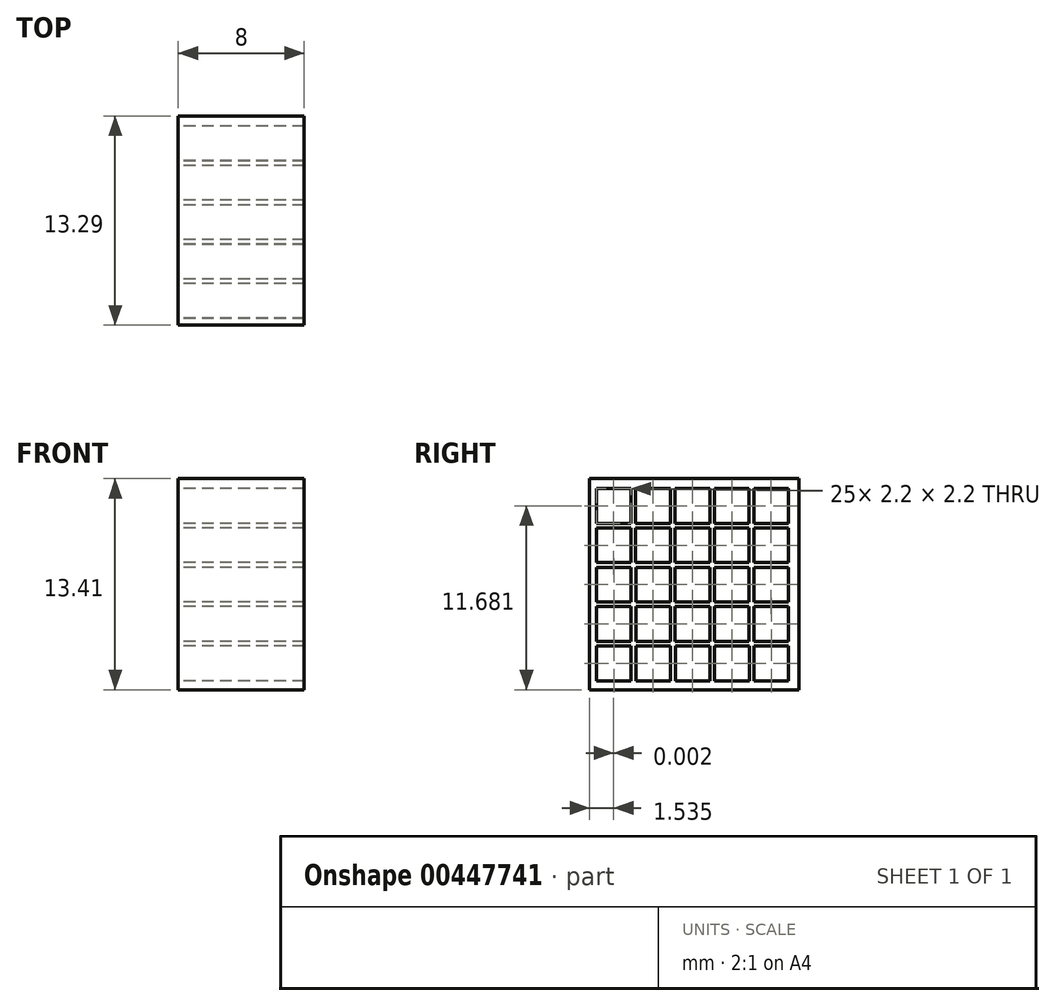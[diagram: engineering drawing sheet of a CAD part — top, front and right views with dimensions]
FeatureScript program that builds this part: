
annotation { "Feature Type Name" : "Feature", "Feature Type Description" : "" }
export const myFeature = defineFeature(function(context is Context, id is Id, definition is map)
    precondition{}
    {
        {
            var Q0;
            Q0=qCreatedBy(makeId("Right.planeOp"),FACE);
            var sketch = newSketch(context, id + "F0", { "sketchPlane" : qUnion([Q0])});
            skLineSegment(sketch, "E0.bottom", {"start": v(-0.5, -2.47) * mm, "end": v(1.7, -2.47) * mm});
            skLineSegment(sketch, "E0.top", {"start": v(-0.5, -4.67) * mm, "end": v(1.7, -4.67) * mm});
            skLineSegment(sketch, "E0.left", {"start": v(-0.5, -2.47) * mm, "end": v(-0.5, -4.67) * mm});
            skLineSegment(sketch, "E0.right", {"start": v(1.7, -2.47) * mm, "end": v(1.7, -4.67) * mm});
            skLineSegment(sketch, "E1.1.0.0", {"start": v(4.2, -2.47) * mm, "end": v(4.2, -4.67) * mm});
            skLineSegment(sketch, "E1.1.0.1", {"start": v(2, -2.47) * mm, "end": v(2, -4.67) * mm});
            skLineSegment(sketch, "E1.1.0.2", {"start": v(2, -4.67) * mm, "end": v(4.2, -4.67) * mm});
            skLineSegment(sketch, "E1.1.0.3", {"start": v(2, -2.47) * mm, "end": v(4.2, -2.47) * mm});
            skLineSegment(sketch, "E1.2.0.0", {"start": v(6.7, -2.47) * mm, "end": v(6.7, -4.67) * mm});
            skLineSegment(sketch, "E1.2.0.1", {"start": v(4.5, -2.47) * mm, "end": v(4.5, -4.67) * mm});
            skLineSegment(sketch, "E1.2.0.2", {"start": v(4.5, -4.67) * mm, "end": v(6.7, -4.67) * mm});
            skLineSegment(sketch, "E1.2.0.3", {"start": v(4.5, -2.47) * mm, "end": v(6.7, -2.47) * mm});
            skLineSegment(sketch, "E1.3.0.0", {"start": v(9.2, -2.47) * mm, "end": v(9.2, -4.67) * mm});
            skLineSegment(sketch, "E1.3.0.1", {"start": v(7, -2.47) * mm, "end": v(7, -4.67) * mm});
            skLineSegment(sketch, "E1.3.0.2", {"start": v(7, -4.67) * mm, "end": v(9.2, -4.67) * mm});
            skLineSegment(sketch, "E1.3.0.3", {"start": v(7, -2.47) * mm, "end": v(9.2, -2.47) * mm});
            skLineSegment(sketch, "E1.4.0.0", {"start": v(11.7, -2.47) * mm, "end": v(11.7, -4.67) * mm});
            skLineSegment(sketch, "E1.4.0.1", {"start": v(9.5, -2.47) * mm, "end": v(9.5, -4.67) * mm});
            skLineSegment(sketch, "E1.4.0.2", {"start": v(9.5, -4.67) * mm, "end": v(11.7, -4.67) * mm});
            skLineSegment(sketch, "E1.4.0.3", {"start": v(9.5, -2.47) * mm, "end": v(11.7, -2.47) * mm});
            skLineSegment(sketch, "E2.1.0.0", {"start": v(11.7, -4.97) * mm, "end": v(11.7, -7.17) * mm});
            skLineSegment(sketch, "E2.1.0.1", {"start": v(9.5, -7.17) * mm, "end": v(11.7, -7.17) * mm});
            skLineSegment(sketch, "E2.1.0.3", {"start": v(9.2, -4.97) * mm, "end": v(9.2, -7.17) * mm});
            skLineSegment(sketch, "E2.1.0.4", {"start": v(4.5, -4.97) * mm, "end": v(6.7, -4.97) * mm});
            skLineSegment(sketch, "E2.1.0.5", {"start": v(4.5, -7.17) * mm, "end": v(6.7, -7.17) * mm});
            skLineSegment(sketch, "E2.1.0.6", {"start": v(4.5, -4.97) * mm, "end": v(4.5, -7.17) * mm});
            skLineSegment(sketch, "E2.1.0.7", {"start": v(6.7, -4.97) * mm, "end": v(6.7, -7.17) * mm});
            skLineSegment(sketch, "E2.1.0.8", {"start": v(2, -4.97) * mm, "end": v(4.2, -4.97) * mm});
            skLineSegment(sketch, "E2.1.0.9", {"start": v(2, -7.17) * mm, "end": v(4.2, -7.17) * mm});
            skLineSegment(sketch, "E2.1.0.10", {"start": v(4.2, -4.97) * mm, "end": v(4.2, -7.17) * mm});
            skLineSegment(sketch, "E2.1.0.11", {"start": v(-0.5, -4.97) * mm, "end": v(-0.5, -7.17) * mm});
            skLineSegment(sketch, "E2.1.0.12", {"start": v(-0.5, -4.97) * mm, "end": v(1.7, -4.97) * mm});
            skLineSegment(sketch, "E2.1.0.13", {"start": v(7, -4.97) * mm, "end": v(9.2, -4.97) * mm});
            skLineSegment(sketch, "E2.1.0.14", {"start": v(7, -7.17) * mm, "end": v(9.2, -7.17) * mm});
            skLineSegment(sketch, "E2.1.0.15", {"start": v(7, -4.97) * mm, "end": v(7, -7.17) * mm});
            skLineSegment(sketch, "E2.1.0.16", {"start": v(9.5, -4.97) * mm, "end": v(9.5, -7.17) * mm});
            skLineSegment(sketch, "E2.1.0.17", {"start": v(9.5, -4.97) * mm, "end": v(11.7, -4.97) * mm});
            skLineSegment(sketch, "E2.1.0.18", {"start": v(1.7, -4.97) * mm, "end": v(1.7, -7.17) * mm});
            skLineSegment(sketch, "E2.1.0.19", {"start": v(-0.5, -7.17) * mm, "end": v(1.7, -7.17) * mm});
            skLineSegment(sketch, "E2.2.0.0", {"start": v(11.7, -7.47) * mm, "end": v(11.7, -9.67) * mm});
            skLineSegment(sketch, "E2.2.0.1", {"start": v(9.5, -9.67) * mm, "end": v(11.7, -9.67) * mm});
            skLineSegment(sketch, "E2.2.0.2", {"start": v(-0.5, -9.67) * mm, "end": v(2, -9.67) * mm, "construction": true});
            skLineSegment(sketch, "E2.2.0.3", {"start": v(9.2, -7.47) * mm, "end": v(9.2, -9.67) * mm});
            skLineSegment(sketch, "E2.2.0.4", {"start": v(4.5, -7.47) * mm, "end": v(6.7, -7.47) * mm});
            skLineSegment(sketch, "E2.2.0.5", {"start": v(4.5, -9.67) * mm, "end": v(6.7, -9.67) * mm});
            skLineSegment(sketch, "E2.2.0.6", {"start": v(4.5, -7.47) * mm, "end": v(4.5, -9.67) * mm});
            skLineSegment(sketch, "E2.2.0.7", {"start": v(6.7, -7.47) * mm, "end": v(6.7, -9.67) * mm});
            skLineSegment(sketch, "E2.2.0.8", {"start": v(2, -7.47) * mm, "end": v(4.2, -7.47) * mm});
            skLineSegment(sketch, "E2.2.0.9", {"start": v(2, -9.67) * mm, "end": v(4.2, -9.67) * mm});
            skLineSegment(sketch, "E2.2.0.10", {"start": v(4.2, -7.47) * mm, "end": v(4.2, -9.67) * mm});
            skLineSegment(sketch, "E2.2.0.11", {"start": v(-0.5, -7.47) * mm, "end": v(-0.5, -9.67) * mm});
            skLineSegment(sketch, "E2.2.0.12", {"start": v(-0.5, -7.47) * mm, "end": v(1.7, -7.47) * mm});
            skLineSegment(sketch, "E2.2.0.13", {"start": v(7, -7.47) * mm, "end": v(9.2, -7.47) * mm});
            skLineSegment(sketch, "E2.2.0.14", {"start": v(7, -9.67) * mm, "end": v(9.2, -9.67) * mm});
            skLineSegment(sketch, "E2.2.0.15", {"start": v(7, -7.47) * mm, "end": v(7, -9.67) * mm});
            skLineSegment(sketch, "E2.2.0.16", {"start": v(9.5, -7.47) * mm, "end": v(9.5, -9.67) * mm});
            skLineSegment(sketch, "E2.2.0.17", {"start": v(9.5, -7.47) * mm, "end": v(11.7, -7.47) * mm});
            skLineSegment(sketch, "E2.2.0.18", {"start": v(1.7, -7.47) * mm, "end": v(1.7, -9.67) * mm});
            skLineSegment(sketch, "E2.2.0.19", {"start": v(-0.5, -9.67) * mm, "end": v(1.7, -9.67) * mm});
            skLineSegment(sketch, "E2.3.0.0", {"start": v(11.7, -9.97) * mm, "end": v(11.7, -12.17) * mm});
            skLineSegment(sketch, "E2.3.0.1", {"start": v(9.5, -12.17) * mm, "end": v(11.7, -12.17) * mm});
            skLineSegment(sketch, "E2.3.0.3", {"start": v(9.2, -9.97) * mm, "end": v(9.2, -12.17) * mm});
            skLineSegment(sketch, "E2.3.0.4", {"start": v(4.5, -9.97) * mm, "end": v(6.7, -9.97) * mm});
            skLineSegment(sketch, "E2.3.0.5", {"start": v(4.5, -12.17) * mm, "end": v(6.7, -12.17) * mm});
            skLineSegment(sketch, "E2.3.0.6", {"start": v(4.5, -9.97) * mm, "end": v(4.5, -12.17) * mm});
            skLineSegment(sketch, "E2.3.0.7", {"start": v(6.7, -9.97) * mm, "end": v(6.7, -12.17) * mm});
            skLineSegment(sketch, "E2.3.0.8", {"start": v(2, -9.97) * mm, "end": v(4.2, -9.97) * mm});
            skLineSegment(sketch, "E2.3.0.9", {"start": v(2, -12.17) * mm, "end": v(4.2, -12.17) * mm});
            skLineSegment(sketch, "E2.3.0.10", {"start": v(4.2, -9.97) * mm, "end": v(4.2, -12.17) * mm});
            skLineSegment(sketch, "E2.3.0.11", {"start": v(-0.5, -9.97) * mm, "end": v(-0.5, -12.17) * mm});
            skLineSegment(sketch, "E2.3.0.12", {"start": v(-0.5, -9.97) * mm, "end": v(1.7, -9.97) * mm});
            skLineSegment(sketch, "E2.3.0.13", {"start": v(7, -9.97) * mm, "end": v(9.2, -9.97) * mm});
            skLineSegment(sketch, "E2.3.0.14", {"start": v(7, -12.17) * mm, "end": v(9.2, -12.17) * mm});
            skLineSegment(sketch, "E2.3.0.15", {"start": v(7, -9.97) * mm, "end": v(7, -12.17) * mm});
            skLineSegment(sketch, "E2.3.0.16", {"start": v(9.5, -9.97) * mm, "end": v(9.5, -12.17) * mm});
            skLineSegment(sketch, "E2.3.0.17", {"start": v(9.5, -9.97) * mm, "end": v(11.7, -9.97) * mm});
            skLineSegment(sketch, "E2.3.0.18", {"start": v(1.7, -9.97) * mm, "end": v(1.7, -12.17) * mm});
            skLineSegment(sketch, "E2.3.0.19", {"start": v(-0.5, -12.17) * mm, "end": v(1.7, -12.17) * mm});
            skLineSegment(sketch, "E2.4.0.0", {"start": v(11.7, -12.47) * mm, "end": v(11.7, -14.67) * mm});
            skLineSegment(sketch, "E2.4.0.1", {"start": v(9.5, -14.67) * mm, "end": v(11.7, -14.67) * mm});
            skLineSegment(sketch, "E2.4.0.2", {"start": v(-0.5, -14.67) * mm, "end": v(2, -14.67) * mm, "construction": true});
            skLineSegment(sketch, "E2.4.0.3", {"start": v(9.2, -12.47) * mm, "end": v(9.2, -14.67) * mm});
            skLineSegment(sketch, "E2.4.0.4", {"start": v(4.5, -12.47) * mm, "end": v(6.7, -12.47) * mm});
            skLineSegment(sketch, "E2.4.0.5", {"start": v(4.5, -14.67) * mm, "end": v(6.7, -14.67) * mm});
            skLineSegment(sketch, "E2.4.0.6", {"start": v(4.5, -12.47) * mm, "end": v(4.5, -14.67) * mm});
            skLineSegment(sketch, "E2.4.0.7", {"start": v(6.7, -12.47) * mm, "end": v(6.7, -14.67) * mm});
            skLineSegment(sketch, "E2.4.0.8", {"start": v(2, -12.47) * mm, "end": v(4.2, -12.47) * mm});
            skLineSegment(sketch, "E2.4.0.9", {"start": v(2, -14.67) * mm, "end": v(4.2, -14.67) * mm});
            skLineSegment(sketch, "E2.4.0.10", {"start": v(4.2, -12.47) * mm, "end": v(4.2, -14.67) * mm});
            skLineSegment(sketch, "E2.4.0.11", {"start": v(-0.5, -12.47) * mm, "end": v(-0.5, -14.67) * mm});
            skLineSegment(sketch, "E2.4.0.12", {"start": v(-0.5, -12.47) * mm, "end": v(1.7, -12.47) * mm});
            skLineSegment(sketch, "E2.4.0.13", {"start": v(7, -12.47) * mm, "end": v(9.2, -12.47) * mm});
            skLineSegment(sketch, "E2.4.0.14", {"start": v(7, -14.67) * mm, "end": v(9.2, -14.67) * mm});
            skLineSegment(sketch, "E2.4.0.15", {"start": v(7, -12.47) * mm, "end": v(7, -14.67) * mm});
            skLineSegment(sketch, "E2.4.0.16", {"start": v(9.5, -12.47) * mm, "end": v(9.5, -14.67) * mm});
            skLineSegment(sketch, "E2.4.0.17", {"start": v(9.5, -12.47) * mm, "end": v(11.7, -12.47) * mm});
            skLineSegment(sketch, "E2.4.0.18", {"start": v(1.7, -12.47) * mm, "end": v(1.7, -14.67) * mm});
            skLineSegment(sketch, "E2.4.0.19", {"start": v(-0.5, -14.67) * mm, "end": v(1.7, -14.67) * mm});
            skLineSegment(sketch, "E2.direction1", {"start": v(-0.5, -4.67) * mm, "end": v(-0.5, -7.17) * mm, "construction": true});
            skLineSegment(sketch, "E3.bottom", {"start": v(-0.94, -1.84) * mm, "end": v(12.35, -1.84) * mm});
            skLineSegment(sketch, "E3.top", {"start": v(-0.94, -15.25) * mm, "end": v(12.35, -15.25) * mm});
            skLineSegment(sketch, "E3.left", {"start": v(-0.94, -1.84) * mm, "end": v(-0.94, -15.25) * mm});
            skLineSegment(sketch, "E3.right", {"start": v(12.35, -1.84) * mm, "end": v(12.35, -15.25) * mm});
            skLineSegment(sketch, "E4", {"start": v(2, -4.97) * mm, "end": v(2, -7.17) * mm});
            skLineSegment(sketch, "E5", {"start": v(2, -7.47) * mm, "end": v(2, -9.67) * mm});
            skLineSegment(sketch, "E6", {"start": v(2, -9.97) * mm, "end": v(2, -12.17) * mm});
            skLineSegment(sketch, "E7", {"start": v(2, -12.47) * mm, "end": v(2, -14.67) * mm});
            skSolve(sketch);
        }
        {
            var Q0;
            Q0 = qSketchRegion(id + "F0", true);
            extrude(context, id + "F1", {"entities" : qUnion([Q0]), "depth" : 8 * mm});
        }
    });
